# Revit family: HTT31-3D
name_source: partatom
category: Structural Connections
revit_build: Autodesk Revit 2014 (Build: 20130308_1515(x64)
units: mm (PartAtom-declared; Revit-internal decimal feet)

## types (1)
- HTT31-3D
    A = 793 mm  [stored 2.60171 ft]
    B = 57 mm  [stored 0.187008 ft]
    C = 54 mm  [stored 0.177165 ft]
    D = 12 mm  [stored 0.0393701 ft]
    Default Elevation = 0 mm  [stored 0 ft]
    Description = Holdown
    E = 33 mm  [stored 0.108268 ft]
    F = 80 mm  [stored 0.262467 ft]
    Manufacturer = Simpson Strong-Tie Company Inc.
    Model = HTT31
    Model Disclaimer = Contact Simpson Strong-Tie Company Inc. for more information
    Product Type = Holdown
    Provide Feedback = http://www.strongtie.com
    URL = http://www.strongtie.eu
    t = 3 mm  [stored 0.00984252 ft]

note: [stored X ft] marks values corroborated as IEEE doubles in the binary element streams (Revit-internal decimal feet)

## geometry (parser evidence)
native form markers: Blend x83, Sweep x1
no freeform markers — native parametric forms only
